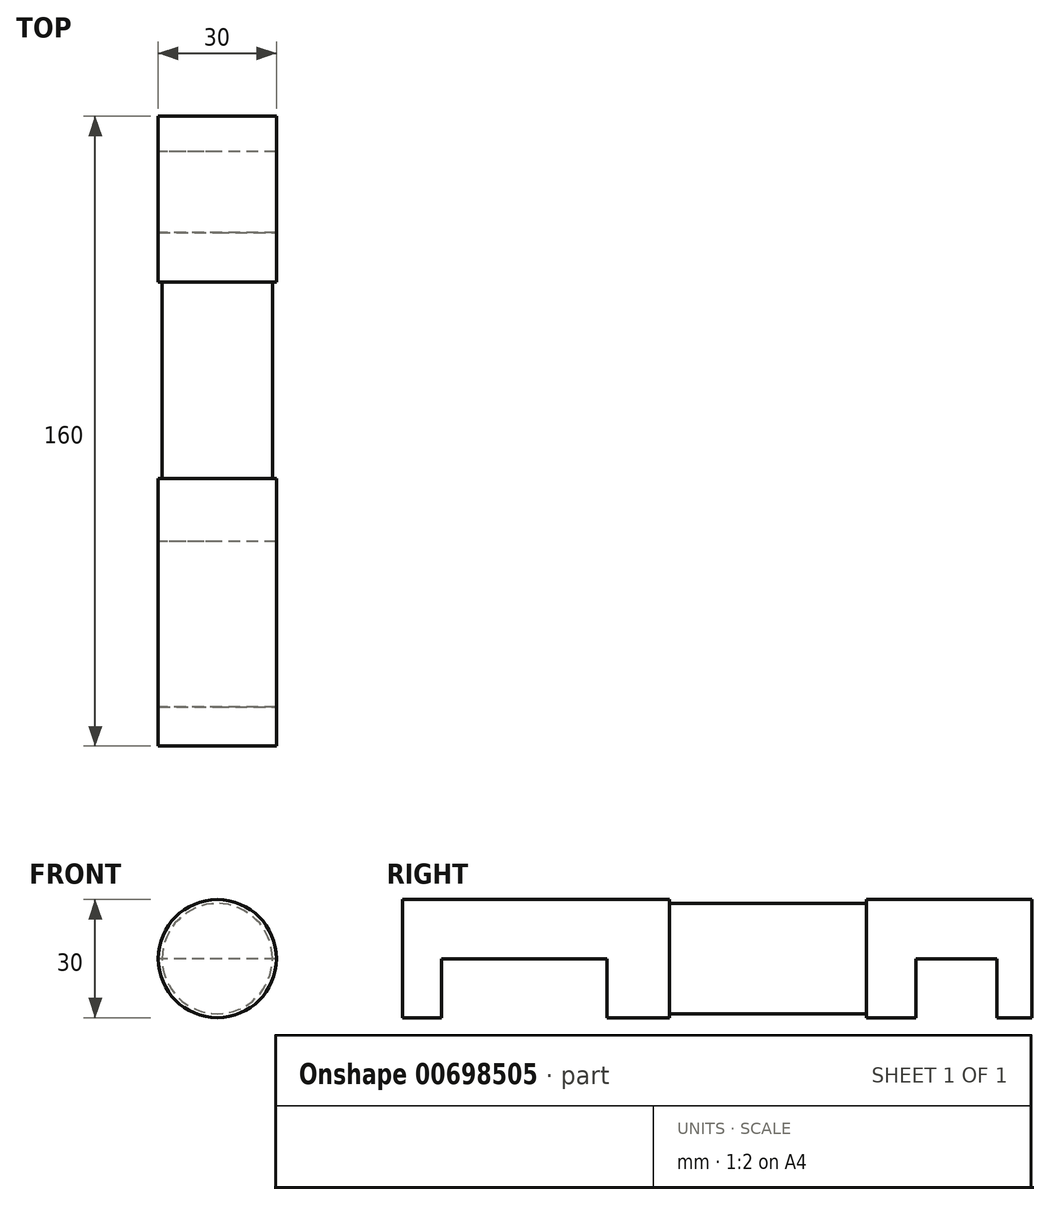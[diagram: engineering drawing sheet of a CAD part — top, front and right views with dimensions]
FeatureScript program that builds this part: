
annotation { "Feature Type Name" : "Feature", "Feature Type Description" : "" }
export const myFeature = defineFeature(function(context is Context, id is Id, definition is map)
    precondition{}
    {
        {
            var Q0;
            Q0=qCreatedBy(makeId("Front.planeOp"),FACE);
            var sketch = newSketch(context, id + "F0", { "sketchPlane" : qUnion([Q0])});
            skCircle(sketch, "E0", {"center": v(0, 0) * mm, "radius": 15 * mm});
            skSolve(sketch);
        }
        {
            var Q0;
            Q0 = qSketchRegion(id + "F0", true);
            var Q1;
            Q1=makeQuery(id+"F0.imprint","IMPRINT",FACE,{"disambiguationData":[TD([[makeQuery(id+"F0.imprint","IMPRINT",EDGE,{"derivedFrom":sQuery(id+"F0.wireOp",EDGE,"E0")}),1.0]])]});
            extrude(context, id + "F1", {"entities" : qUnion([Q0, Q1]), "depth" : 160 * mm, "offsetDistance" : 25 * mm});
        }
        {
            var Q0;
            Q0=qCreatedBy(makeId("Right.planeOp"),FACE);
            var sketch = newSketch(context, id + "F2", { "sketchPlane" : qUnion([Q0])});
            skLineSegment(sketch, "E1", {"start": v(0, 0) * mm, "end": v(-10, 0) * mm, "construction": true});
            skLineSegment(sketch, "E2", {"start": v(-10, 0) * mm, "end": v(-10, -15) * mm});
            skLineSegment(sketch, "E3", {"start": v(-10, -15) * mm, "end": v(-28.5, -15) * mm});
            skLineSegment(sketch, "E4", {"start": v(-28.5, -15) * mm, "end": v(-28.5, 0) * mm});
            skLineSegment(sketch, "E5", {"start": v(-28.5, 0) * mm, "end": v(-10, 0) * mm});
            skLineSegment(sketch, "E6", {"start": v(-28.5, 0) * mm, "end": v(-110, 0) * mm, "construction": true});
            skLineSegment(sketch, "E7", {"start": v(-110, 0) * mm, "end": v(-110, -15) * mm});
            skLineSegment(sketch, "E8", {"start": v(-110, -15) * mm, "end": v(-150, -15) * mm});
            skLineSegment(sketch, "E9", {"start": v(-150, -15) * mm, "end": v(-150, 0) * mm});
            skLineSegment(sketch, "E10", {"start": v(-150, 0) * mm, "end": v(-110, 0) * mm});
            skLineSegment(sketch, "E11", {"start": v(-110, 0) * mm, "end": v(-94.25, 0) * mm, "construction": true});
            skSolve(sketch);
        }
        {
            var Q0;
            Q0=makeQuery(id+"F2.imprint","IMPRINT",FACE,{"disambiguationData":[TD([[makeQuery(id+"F2.imprint","IMPRINT",EDGE,{"derivedFrom":sQuery(id+"F2.wireOp",EDGE,"E7")}),-1.0]])]});
            var Q1;
            Q1=makeQuery(id+"F2.imprint","IMPRINT",FACE,{"disambiguationData":[TD([[makeQuery(id+"F2.imprint","IMPRINT",EDGE,{"derivedFrom":sQuery(id+"F2.wireOp",EDGE,"E2")}),-1.0]])]});
            extrude(context, id + "F3", {"entities" : qUnion([Q0, Q1]), "operationType" : NewBodyOperationType.REMOVE, "endBound" : BoundingType.SYMMETRIC, "depth" : 30 * mm, "offsetDistance" : 25 * mm});
        }
        {
            var Q0;
            Q0=makeQuery(id+"F2.imprint","IMPRINT",FACE,{"disambiguationData":[TD([[makeQuery(id+"F2.imprint","IMPRINT",EDGE,{"derivedFrom":sQuery(id+"F2.wireOp",EDGE,"E2")}),-1.0]])]});
            var Q1;
            Q1=makeQuery(id+"F2.imprint","IMPRINT",FACE,{"disambiguationData":[TD([[makeQuery(id+"F2.imprint","IMPRINT",EDGE,{"derivedFrom":sQuery(id+"F2.wireOp",EDGE,"E7")}),-1.0]])]});
            extrude(context, id + "F4", {"entities" : qUnion([Q0, Q1]), "operationType" : NewBodyOperationType.REMOVE, "endBound" : BoundingType.SYMMETRIC, "oppositeDirection" : true, "depth" : 25 * mm, "offsetDistance" : 25 * mm});
        }
        {
            var Q0;
            Q0=makeQuery(id+"F3.boolean.opBoolean","COPY",FACE,{"derivedFrom":makeQuery(id+"F3.opExtrude","SWEPT_FACE",FACE,{"disambiguationData":[OSD([sQuery(id+"F2.wireOp",EDGE,"E7")])]})});
            extrude(context, id + "F5", {"entities" : qUnion([Q0]), "operationType" : NewBodyOperationType.REMOVE, "oppositeDirection" : true, "depth" : 2 * mm, "offsetDistance" : 25 * mm});
        }
        {
            var Q0;
            Q0=makeQuery(id+"F3.boolean.opBoolean","COPY",FACE,{"derivedFrom":makeQuery(id+"F3.opExtrude","SWEPT_FACE",FACE,{"disambiguationData":[OSD([sQuery(id+"F2.wireOp",EDGE,"E4")])]})});
            extrude(context, id + "F6", {"entities" : qUnion([Q0]), "operationType" : NewBodyOperationType.REMOVE, "oppositeDirection" : true, "depth" : 1 * mm, "offsetDistance" : 25 * mm});
        }
        {
            var Q0;
            Q0=makeQuery(id+"F3.boolean.opBoolean","COPY",FACE,{"derivedFrom":makeQuery(id+"F3.opExtrude","SWEPT_FACE",FACE,{"disambiguationData":[OSD([sQuery(id+"F2.wireOp",EDGE,"E2")])]})});
            extrude(context, id + "F7", {"entities" : qUnion([Q0]), "operationType" : NewBodyOperationType.REMOVE, "oppositeDirection" : true, "depth" : 1 * mm, "offsetDistance" : 25 * mm});
        }
        {
            var Q0;
            Q0=qCreatedBy(makeId("Right.planeOp"),FACE);
            var sketch = newSketch(context, id + "F8", { "sketchPlane" : qUnion([Q0])});
            skLineSegment(sketch, "E12", {"start": v(-107.82, 0) * mm, "end": v(-107.82, 15) * mm, "construction": true});
            skLineSegment(sketch, "E13", {"start": v(-107.82, 15) * mm, "end": v(-92.07, 15) * mm, "construction": true});
            skLineSegment(sketch, "E14", {"start": v(-92.07, 15) * mm, "end": v(-92.07, 14) * mm});
            skLineSegment(sketch, "E15", {"start": v(-92.07, 14) * mm, "end": v(-42.07, 14) * mm});
            skLineSegment(sketch, "E16", {"start": v(-42.07, 14) * mm, "end": v(-42.07, 15) * mm});
            skLineSegment(sketch, "E17", {"start": v(-42.07, 15) * mm, "end": v(-92.07, 15) * mm});
            skLineSegment(sketch, "E18", {"start": v(0, 0) * mm, "end": v(-161, 0) * mm, "construction": true});
            skSolve(sketch);
        }
        {
            var Q0;
            Q0 = qSketchRegion(id + "F8", true);
            var Q1;
            Q1=sQuery(id+"F8.wireOp",EDGE,"E18");
            revolve(context, id + "F9", {"operationType" : NewBodyOperationType.REMOVE, "entities" : qUnion([Q0]), "axis" : qUnion([Q1]), "revolveType" : RevolveType.FULL, "oppositeDirection" : true});
        }
    });
